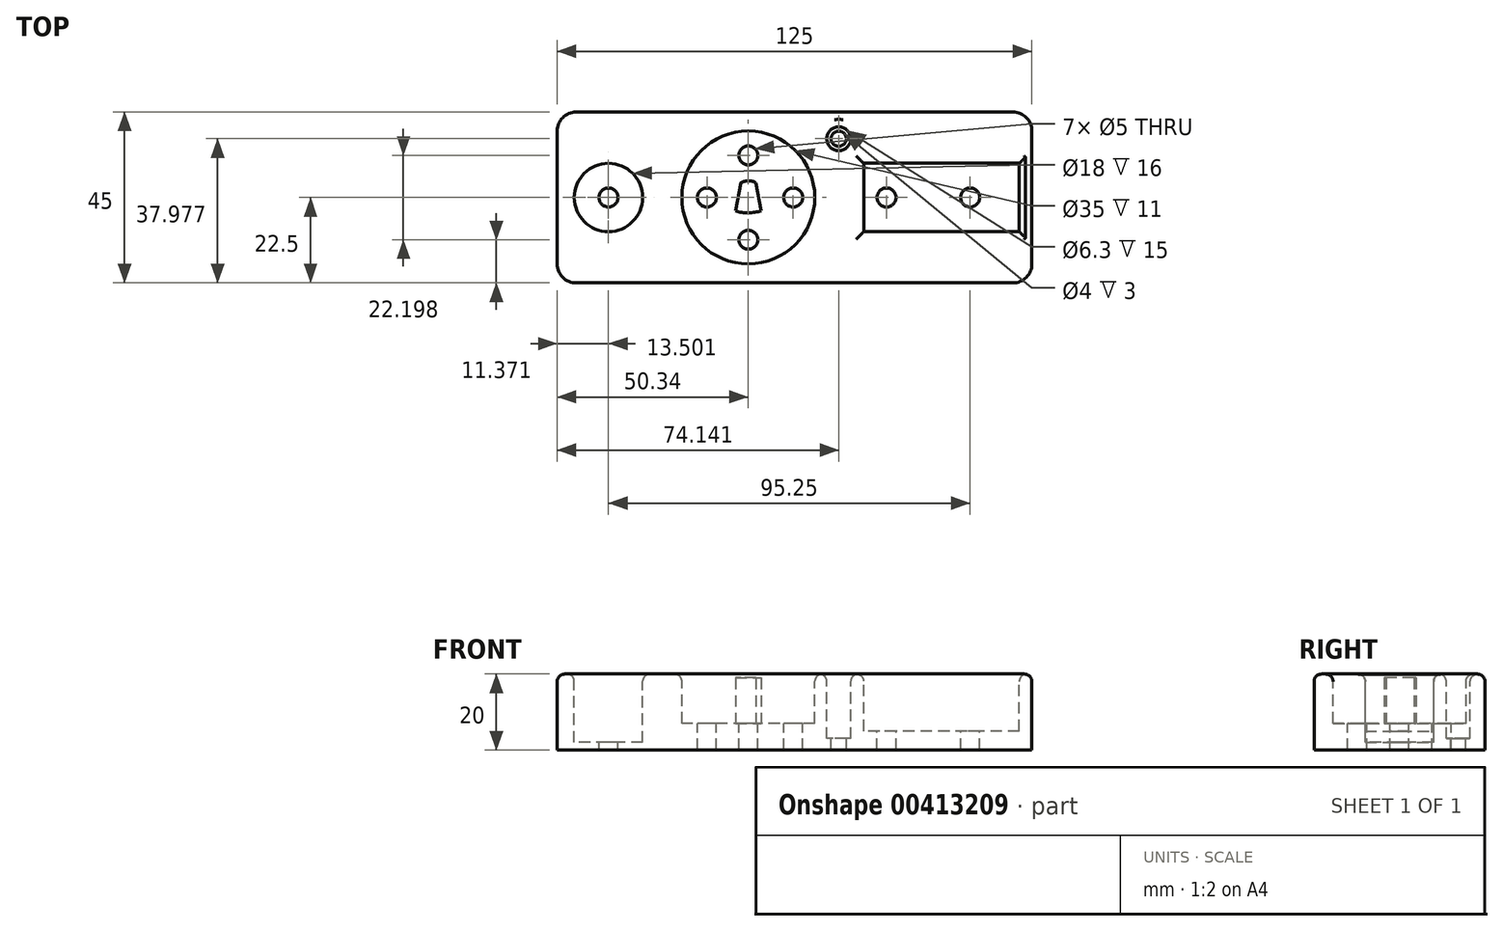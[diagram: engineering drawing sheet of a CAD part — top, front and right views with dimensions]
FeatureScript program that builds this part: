
annotation { "Feature Type Name" : "Feature", "Feature Type Description" : "" }
export const myFeature = defineFeature(function(context is Context, id is Id, definition is map)
    precondition{}
    {
        {
            var Q0;
            Q0=qCreatedBy(makeId("Top.planeOp"),FACE);
            var sketch = newSketch(context, id + "F0", { "sketchPlane" : qUnion([Q0])});
            skLineSegment(sketch, "E0", {"start": v(-50.34, 0) * mm, "end": v(-50.34, 22.5) * mm});
            skLineSegment(sketch, "E1", {"start": v(-50.34, 22.5) * mm, "end": v(74.66, 22.5) * mm});
            skLineSegment(sketch, "E2", {"start": v(74.66, 22.5) * mm, "end": v(74.66, -22.5) * mm});
            skLineSegment(sketch, "E3", {"start": v(74.66, -22.5) * mm, "end": v(-50.34, -22.5) * mm});
            skLineSegment(sketch, "E4", {"start": v(-50.34, -22.5) * mm, "end": v(-50.34, 0) * mm});
            skSolve(sketch);
        }
        {
            var Q0;
            Q0=makeQuery(id+"F0.imprint","IMPRINT",FACE,{"disambiguationData":[TD([[makeQuery(id+"F0.imprint","IMPRINT",EDGE,{"derivedFrom":sQuery(id+"F0.wireOp",EDGE,"E0")}),-1.0]])]});
            extrude(context, id + "F1", {"entities" : qUnion([Q0]), "depth" : 20 * mm});
        }
        {
            var Q0;
            Q0=makeQuery(id+"F1.opExtrude","CAP_FACE",FACE,{"disambiguationData":[OSD([sQuery(id+"F0.wireOp",EDGE,"E0"),sQuery(id+"F0.wireOp",EDGE,"E1"),sQuery(id+"F0.wireOp",EDGE,"E2"),sQuery(id+"F0.wireOp",EDGE,"E3"),sQuery(id+"F0.wireOp",EDGE,"E4")])],"isStart":false});
            cPlane(context, id + "F2", {"entities" : qUnion([Q0]), "cplaneType" : CPlaneType.OFFSET, "offset" : 0 * mm, "width" : 150 * mm, "height" : 150 * mm});
        }
        {
            var Q0;
            Q0=qCreatedBy(id+"F2.planeOp",FACE);
            var sketch = newSketch(context, id + "F3", { "sketchPlane" : qUnion([Q0])});
            skCircle(sketch, "E5", {"center": v(-36.84, 0) * mm, "radius": 9 * mm});
            skSolve(sketch);
        }
        {
            var Q0;
            Q0=makeQuery(id+"F3.imprint","IMPRINT",FACE,{"disambiguationData":[TD([[makeQuery(id+"F3.imprint","IMPRINT",EDGE,{"derivedFrom":sQuery(id+"F3.wireOp",EDGE,"E5")}),1.0]])]});
            extrude(context, id + "F4", {"entities" : qUnion([Q0]), "operationType" : NewBodyOperationType.REMOVE, "oppositeDirection" : true, "depth" : 18 * mm});
        }
        {
            var Q0;
            Q0=makeQuery(id+"F1.opExtrude","CAP_FACE",FACE,{"disambiguationData":[OSD([sQuery(id+"F0.wireOp",EDGE,"E0"),sQuery(id+"F0.wireOp",EDGE,"E1"),sQuery(id+"F0.wireOp",EDGE,"E2"),sQuery(id+"F0.wireOp",EDGE,"E3"),sQuery(id+"F0.wireOp",EDGE,"E4")])],"isStart":false});
            var sketch = newSketch(context, id + "F5", { "sketchPlane" : qUnion([Q0])});
            skCircle(sketch, "E6", {"center": v(0, 0) * mm, "radius": 17.5 * mm});
            skSolve(sketch);
        }
        {
            var Q0;
            Q0=makeQuery(id+"F5.imprint","IMPRINT",FACE,{"disambiguationData":[TD([[makeQuery(id+"F5.imprint","IMPRINT",EDGE,{"derivedFrom":sQuery(id+"F5.wireOp",EDGE,"E6")}),1.0]])]});
            extrude(context, id + "F6", {"entities" : qUnion([Q0]), "operationType" : NewBodyOperationType.REMOVE, "oppositeDirection" : true, "depth" : 13 * mm});
        }
        {
            var Q0;
            Q0=makeQuery(id+"F6.boolean.opBoolean","COPY",FACE,{"derivedFrom":makeQuery(id+"F6.opExtrude","CAP_FACE",FACE,{"disambiguationData":[OSD([sQuery(id+"F5.wireOp",EDGE,"E6")])],"isStart":false})});
            var sketch = newSketch(context, id + "F7", { "sketchPlane" : qUnion([Q0])});
            skPoint(sketch, "E7.end.orphan", {"position": v(0, 0) * mm});
            skArc(sketch, "E8", {"start": v(2, 3.87) * mm, "mid": v(0.03, 4.4) * mm, "end": v(-1.95, 3.9) * mm});
            skPoint(sketch, "E9.start.orphan", {"position": v(0, 3.97) * mm});
            skArc(sketch, "E10", {"start": v(-3.42, -3.55) * mm, "mid": v(0, -4.05) * mm, "end": v(3.4, -3.5) * mm});
            skPoint(sketch, "E11.trimOffspring.start.orphan", {"position": v(0, -3.97) * mm});
            skLineSegment(sketch, "E12", {"start": v(-2.01, 3.81) * mm, "end": v(-3.42, -3.55) * mm});
            skLineSegment(sketch, "E13", {"start": v(2, 3.87) * mm, "end": v(3.4, -3.5) * mm});
            skPoint(sketch, "E14.start.orphan", {"position": v(0, 4.4) * mm});
            skPoint(sketch, "E15.visualSharp", {"position": v(-2, 3.87) * mm});
            skArc(sketch, "E15.filletArc", {"start": v(-1.95, 3.9) * mm, "mid": v(-1.99, 3.87) * mm, "end": v(-2.01, 3.81) * mm});
            skSolve(sketch);
        }
        {
            var Q0;
            {var subQ1=sQuery(id+"F7.wireOp",EDGE,"LmSsfuK4-SigO-Q7p4-IMTy-4ol10E7Rlw1u");Q0=makeQuery(id+"F7.imprint","IMPRINT",FACE,{"disambiguationData":[TD([[makeQuery(id+"F7.imprint","IMPRINT",EDGE,{"derivedFrom":subQ1}),1.0]])]});}
            var Q1;
            Q1=makeQuery(id+"F7.imprint","IMPRINT",FACE,{"disambiguationData":[TD([[makeQuery(id+"F7.imprint","IMPRINT",EDGE,{"derivedFrom":sQuery(id+"F7.wireOp",EDGE,"E8")}),1.0]])]});
            extrude(context, id + "F8", {"entities" : qUnion([Q0, Q1]), "operationType" : NewBodyOperationType.ADD, "depth" : 12 * mm});
        }
        {
            var Q0;
            Q0=makeQuery(id+"F1.opExtrude","CAP_FACE",FACE,{"disambiguationData":[OSD([sQuery(id+"F0.wireOp",EDGE,"E0"),sQuery(id+"F0.wireOp",EDGE,"E1"),sQuery(id+"F0.wireOp",EDGE,"E2"),sQuery(id+"F0.wireOp",EDGE,"E3"),sQuery(id+"F0.wireOp",EDGE,"E4")])],"isStart":false});
            var sketch = newSketch(context, id + "F9", { "sketchPlane" : qUnion([Q0])});
            skLineSegment(sketch, "E16", {"start": v(30.36, 0) * mm, "end": v(30.36, 9) * mm});
            skLineSegment(sketch, "E17", {"start": v(30.36, 9) * mm, "end": v(71.36, 9) * mm});
            skLineSegment(sketch, "E18", {"start": v(71.36, 9) * mm, "end": v(71.36, 0) * mm});
            skLineSegment(sketch, "E19", {"start": v(71.36, 0) * mm, "end": v(71.36, -9) * mm});
            skLineSegment(sketch, "E20", {"start": v(71.36, -9) * mm, "end": v(30.36, -9) * mm});
            skLineSegment(sketch, "E21", {"start": v(30.36, -9) * mm, "end": v(30.36, 0) * mm});
            skSolve(sketch);
        }
        {
            var Q0;
            Q0=makeQuery(id+"F9.imprint","IMPRINT",FACE,{"disambiguationData":[TD([[makeQuery(id+"F9.imprint","IMPRINT",EDGE,{"derivedFrom":sQuery(id+"F9.wireOp",EDGE,"E16")}),-1.0]])]});
            extrude(context, id + "F10", {"entities" : qUnion([Q0]), "operationType" : NewBodyOperationType.REMOVE, "oppositeDirection" : true, "depth" : 15 * mm});
        }
        {
            var Q0;
            Q0=makeQuery(id+"F1.opExtrude","CAP_FACE",FACE,{"disambiguationData":[OSD([sQuery(id+"F0.wireOp",EDGE,"E0"),sQuery(id+"F0.wireOp",EDGE,"E1"),sQuery(id+"F0.wireOp",EDGE,"E2"),sQuery(id+"F0.wireOp",EDGE,"E3"),sQuery(id+"F0.wireOp",EDGE,"E4")])],"isStart":false});
            var sketch = newSketch(context, id + "F11", { "sketchPlane" : qUnion([Q0])});
            skCircle(sketch, "E22", {"center": v(23.8, 15.48) * mm, "radius": 3.15 * mm});
            skSolve(sketch);
        }
        {
            var Q0;
            Q0=makeQuery(id+"F11.imprint","IMPRINT",FACE,{"disambiguationData":[TD([[makeQuery(id+"F11.imprint","IMPRINT",EDGE,{"derivedFrom":sQuery(id+"F11.wireOp",EDGE,"E22")}),1.0]])]});
            extrude(context, id + "F12", {"entities" : qUnion([Q0]), "operationType" : NewBodyOperationType.REMOVE, "oppositeDirection" : true, "depth" : 17 * mm});
        }
        {
            var Q0;
            Q0=makeQuery(id+"F1.opExtrude","SWEPT_EDGE",EDGE,{"disambiguationData":[OSD([sQuery(id+"F0.wireOp",EDGE,"E2"),sQuery(id+"F0.wireOp",EDGE,"E3")])]});
            var Q1;
            Q1=makeQuery(id+"F1.opExtrude","SWEPT_EDGE",EDGE,{"disambiguationData":[OSD([sQuery(id+"F0.wireOp",EDGE,"E1"),sQuery(id+"F0.wireOp",EDGE,"E2")])]});
            var Q2;
            Q2=makeQuery(id+"F1.opExtrude","SWEPT_EDGE",EDGE,{"disambiguationData":[OSD([sQuery(id+"F0.wireOp",EDGE,"E3"),sQuery(id+"F0.wireOp",EDGE,"E4")])]});
            var Q3;
            Q3=makeQuery(id+"F1.opExtrude","SWEPT_EDGE",EDGE,{"disambiguationData":[OSD([sQuery(id+"F0.wireOp",EDGE,"E0"),sQuery(id+"F0.wireOp",EDGE,"E1")])]});
            fillet(context, id + "F13", {"entities" : qUnion([Q0, Q1, Q2, Q3]), "radius" : 5 * mm, "tangentPropagation" : true, "allowEdgeOverflow" : false});
        }
        {
            var Q0;
            Q0=makeQuery(id+"F1.opExtrude","CAP_FACE",FACE,{"disambiguationData":[OSD([sQuery(id+"F0.wireOp",EDGE,"E0"),sQuery(id+"F0.wireOp",EDGE,"E1"),sQuery(id+"F0.wireOp",EDGE,"E2"),sQuery(id+"F0.wireOp",EDGE,"E3"),sQuery(id+"F0.wireOp",EDGE,"E4")])],"isStart":false});
            fillet(context, id + "F14", {"entities" : qUnion([Q0]), "radius" : 2 * mm, "tangentPropagation" : true, "allowEdgeOverflow" : false});
        }
        {
            var Q0;
            Q0=makeQuery(id+"F4.boolean.opBoolean","COPY",FACE,{"derivedFrom":makeQuery(id+"F4.opExtrude","CAP_FACE",FACE,{"disambiguationData":[OSD([sQuery(id+"F3.wireOp",EDGE,"E5")])],"isStart":false})});
            var sketch = newSketch(context, id + "F15", { "sketchPlane" : qUnion([Q0])});
            skCircle(sketch, "E23", {"center": v(-36.84, 0) * mm, "radius": 2.5 * mm});
            skSolve(sketch);
        }
        {
            var Q0;
            Q0=makeQuery(id+"F15.imprint","IMPRINT",FACE,{"disambiguationData":[TD([[makeQuery(id+"F15.imprint","IMPRINT",EDGE,{"derivedFrom":sQuery(id+"F15.wireOp",EDGE,"E23")}),1.0]])]});
            extrude(context, id + "F16", {"entities" : qUnion([Q0]), "operationType" : NewBodyOperationType.REMOVE, "oppositeDirection" : true, "depth" : 25 * mm});
        }
        {
            var Q0;
            Q0=makeQuery(id+"F6.boolean.opBoolean","COPY",FACE,{"derivedFrom":makeQuery(id+"F6.opExtrude","CAP_FACE",FACE,{"disambiguationData":[OSD([sQuery(id+"F5.wireOp",EDGE,"E6")])],"isStart":false})});
            var sketch = newSketch(context, id + "F17", { "sketchPlane" : qUnion([Q0])});
            skCircle(sketch, "E24", {"center": v(0, 11.07) * mm, "radius": 2.5 * mm});
            skCircle(sketch, "E25", {"center": v(11.8, 0) * mm, "radius": 2.5 * mm});
            skCircle(sketch, "E26", {"center": v(0, -11.13) * mm, "radius": 2.5 * mm});
            skCircle(sketch, "E27", {"center": v(-10.92, 0) * mm, "radius": 2.5 * mm});
            skSolve(sketch);
        }
        {
            var Q0;
            Q0=makeQuery(id+"F17.imprint","IMPRINT",FACE,{"disambiguationData":[TD([[makeQuery(id+"F17.imprint","IMPRINT",EDGE,{"derivedFrom":sQuery(id+"F17.wireOp",EDGE,"E24")}),1.0]])]});
            var Q1;
            Q1=makeQuery(id+"F17.imprint","IMPRINT",FACE,{"disambiguationData":[TD([[makeQuery(id+"F17.imprint","IMPRINT",EDGE,{"derivedFrom":sQuery(id+"F17.wireOp",EDGE,"E27")}),1.0]])]});
            var Q2;
            Q2=makeQuery(id+"F17.imprint","IMPRINT",FACE,{"disambiguationData":[TD([[makeQuery(id+"F17.imprint","IMPRINT",EDGE,{"derivedFrom":sQuery(id+"F17.wireOp",EDGE,"E26")}),1.0]])]});
            var Q3;
            Q3=makeQuery(id+"F17.imprint","IMPRINT",FACE,{"disambiguationData":[TD([[makeQuery(id+"F17.imprint","IMPRINT",EDGE,{"derivedFrom":sQuery(id+"F17.wireOp",EDGE,"E25")}),1.0]])]});
            extrude(context, id + "F18", {"entities" : qUnion([Q0, Q1, Q2, Q3]), "operationType" : NewBodyOperationType.REMOVE, "oppositeDirection" : true, "depth" : 25 * mm});
        }
        {
            var Q0;
            Q0=makeQuery(id+"F12.boolean.opBoolean","COPY",FACE,{"derivedFrom":makeQuery(id+"F12.opExtrude","CAP_FACE",FACE,{"disambiguationData":[OSD([sQuery(id+"F11.wireOp",EDGE,"E22")])],"isStart":false})});
            var sketch = newSketch(context, id + "F19", { "sketchPlane" : qUnion([Q0])});
            skCircle(sketch, "E28", {"center": v(23.8, 15.48) * mm, "radius": 2 * mm});
            skSolve(sketch);
        }
        {
            var Q0;
            Q0=makeQuery(id+"F19.imprint","IMPRINT",FACE,{"disambiguationData":[TD([[makeQuery(id+"F19.imprint","IMPRINT",EDGE,{"derivedFrom":sQuery(id+"F19.wireOp",EDGE,"E28")}),1.0]])]});
            extrude(context, id + "F20", {"entities" : qUnion([Q0]), "operationType" : NewBodyOperationType.REMOVE, "oppositeDirection" : true, "depth" : 25 * mm});
        }
        {
            var Q0;
            Q0=makeQuery(id+"F10.boolean.opBoolean","COPY",FACE,{"derivedFrom":makeQuery(id+"F10.opExtrude","CAP_FACE",FACE,{"disambiguationData":[OSD([sQuery(id+"F9.wireOp",EDGE,"E16"),sQuery(id+"F9.wireOp",EDGE,"E17"),sQuery(id+"F9.wireOp",EDGE,"E18"),sQuery(id+"F9.wireOp",EDGE,"E19"),sQuery(id+"F9.wireOp",EDGE,"E20"),sQuery(id+"F9.wireOp",EDGE,"E21")])],"isStart":false})});
            var sketch = newSketch(context, id + "F21", { "sketchPlane" : qUnion([Q0])});
            skCircle(sketch, "E29", {"center": v(36.38, 0) * mm, "radius": 2.5 * mm});
            skCircle(sketch, "E30", {"center": v(58.41, 0) * mm, "radius": 2.5 * mm});
            skSolve(sketch);
        }
        {
            var Q0;
            Q0=makeQuery(id+"F21.imprint","IMPRINT",FACE,{"disambiguationData":[TD([[makeQuery(id+"F21.imprint","IMPRINT",EDGE,{"derivedFrom":sQuery(id+"F21.wireOp",EDGE,"E29")}),1.0]])]});
            var Q1;
            Q1=makeQuery(id+"F21.imprint","IMPRINT",FACE,{"disambiguationData":[TD([[makeQuery(id+"F21.imprint","IMPRINT",EDGE,{"derivedFrom":sQuery(id+"F21.wireOp",EDGE,"E30")}),1.0]])]});
            extrude(context, id + "F22", {"entities" : qUnion([Q0, Q1]), "operationType" : NewBodyOperationType.REMOVE, "oppositeDirection" : true, "depth" : 25 * mm});
        }
    });
